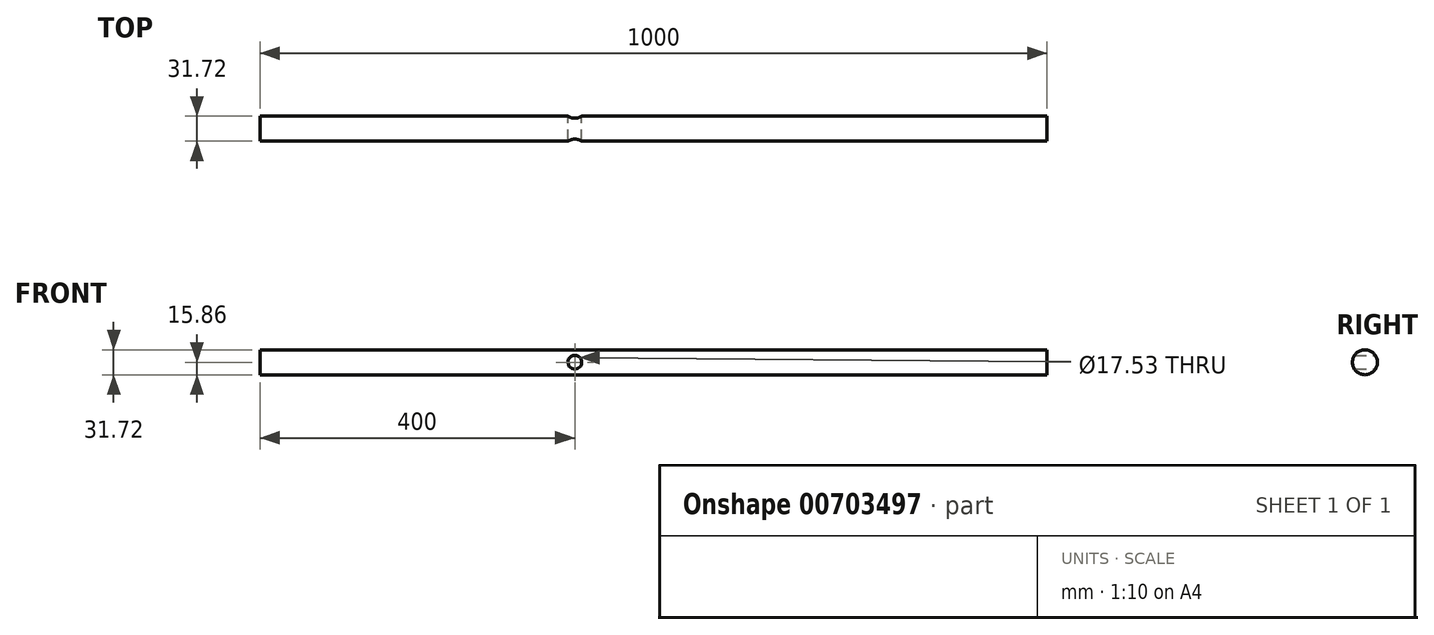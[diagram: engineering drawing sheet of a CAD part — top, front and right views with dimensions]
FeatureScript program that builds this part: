
annotation { "Feature Type Name" : "Feature", "Feature Type Description" : "" }
export const myFeature = defineFeature(function(context is Context, id is Id, definition is map)
    precondition{}
    {
        {
            var Q0;
            Q0=qCreatedBy(makeId("Right.planeOp"),FACE);
            var sketch = newSketch(context, id + "F0", { "sketchPlane" : qUnion([Q0])});
            skCircle(sketch, "E0", {"center": v(0, 0) * mm, "radius": 15.86 * mm});
            skSolve(sketch);
        }
        {
            var Q0;
            Q0 = qSketchRegion(id + "F0", true);
            extrude(context, id + "F1", {"entities" : qUnion([Q0]), "depth" : 1000 * mm, "offsetDistance" : 25 * mm});
        }
        {
            var Q0;
            Q0=qCreatedBy(makeId("Front.planeOp"),FACE);
            var sketch = newSketch(context, id + "F2", { "sketchPlane" : qUnion([Q0])});
            skCircle(sketch, "E1", {"center": v(400, 0) * mm, "radius": 8.77 * mm});
            skSolve(sketch);
        }
        {
            var Q0;
            Q0 = qSketchRegion(id + "F2", true);
            extrude(context, id + "F3", {"entities" : qUnion([Q0]), "operationType" : NewBodyOperationType.REMOVE, "endBound" : BoundingType.SYMMETRIC, "depth" : 50 * mm, "offsetDistance" : 25 * mm});
        }
    });
